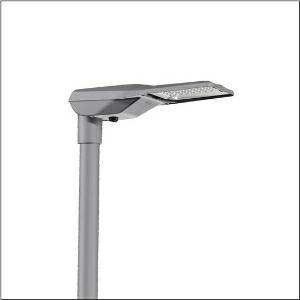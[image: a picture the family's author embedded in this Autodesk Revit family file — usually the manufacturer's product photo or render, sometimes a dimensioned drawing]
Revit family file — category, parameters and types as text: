
# Revit family: streetlight_sl_21_iq_mini___p0_8ab_5xe2r31u08hb_e37e
name_source: partatom
category: Lighting Fixtures
units: mm (PartAtom-declared; Revit-internal decimal feet)

## family parameters
Cut with Voids When Loaded = No
Host = Face
Light Source = No
Part Type = Normal
Room Calculation Point = No
Round Connector Dimension = Use Diameter
Shared = No

## types (1)
- --- (1 x LED, 8460 lm, 71 W, 3000K)
    Apparent Load = 71 VA
    CIE Flux Codes = 36 71 98 100 100
    Color Rendering = 70
    Color Temperature = 3000K
    Default Elevation = 1800 mm
    Description = Streetlight SL 21 iQ mini, mast luminaire, primary light control with lens, of PMMA, primary optical cover: cover, of toughened safety glass, transparent, light distribution: P0.8aB, light emission: direct distribution, primary light characteristic: asymmetric, installation type: post-top, side-entry, LED, High Power LED, rated luminous flux: 8.460lm, luminous efficacy: 119lm/W, light colour: 730, colour temperature: 3000K, control gear: iQ-Street Remote, D4i with power reduction, control: pre-setting: logarithmic dimming characteristic, Street-Remote, Auto-Match, Temp-Guard, Lumen-Switch, Night-Set, Smart-Wire, Light-Fading, Desk-Remote (wireless, voltage-free reading and setting of iQ features in the workshop via application-optimized NFC function/RFID function), optimised constant luminous flux control (CLO 2.0), mains connection: 220..240V, AC, 50/60Hz, start of lifetime: 71W, end of service life: 75W, reduction: 30W, luminaire housing, of diecast aluminium, powder-coated, Siteco® metallic grey (DB 702S), corrosivity category C5 mid according to DIN EN ISO 12944, please order mast flange separately, inclination adjustable: 0°, 5°, 10°, 15°, sealing non-destructively replaceable, multi-level sealing system, length: 628mm, width: 235mm, height: 110mm, mast flange for spigot size: 42mm (side-entry): 5XC10008XM4, 60/48mm (side-entry/post-top): 5XC10108XM2, 76/60mm (side-entry/post-top): 5XC10108XM1, mounting height: 4..8m, Smart Interface below, protection rating (complete): IP66, insulation class (complete): insulation class II (safety insulation), certification: CE, ENEC, ENEC+, VDE, impact resistance: IK09, permissible operating ambient temperature for outdoor applications: -40..+50°C, standard-compliant lighting for roads and squares, packaging unit: 1 piece

Light Distribution: P0.8aB
    Height = 110 mm
    Lamp = 1 x LED
    Lamp Light Flux = 8460 lm
    Lamp Power = 71 W
    Lamp count = 1
    Length = 625 mm
    Luminous efficacy = 119 lm/W
    Manufacturer = Siteco
    ModVariant = No
    Model = 5XE2R31U08HB
    Number of Poles = 1
    OnlyDefault = Yes
    Power Factor = 1
    Product Name = Streetlight SL 21 iQ mini | P0.8aB
    Product group = mast luminaire | pylon top
    ProductGroupID = 6100
    Protection Class = Protection class II
    Protection Degree = IP 66
    RLX_Detail_Level = 1
    RLX_Emergency_Light_Flux = 0 lm
    RLX_Emergency_Type = 0
    RLX_Emergency_Type_DB = No
    RlxData = <blob elided: 93689 chars, md5=c6e5c06a>
    Socket = socket
    Standby Power = 0 W
    System Light Flux = 8460 lm
    System Power = 71 W
    Type Comments = factory setting: luminous flux: 100 % | dim-lin: 254 | 716 mA
    Type Image = l_1003516.jpg
    URL = http://relux.com
    VarID = @adj_072654
    Voltage = 0 V
    Weight = 0.00 kg
    Width = 234 mm

## geometry (parser evidence)
native form markers: Blend x4, Sweep x10
no freeform markers — native parametric forms only
